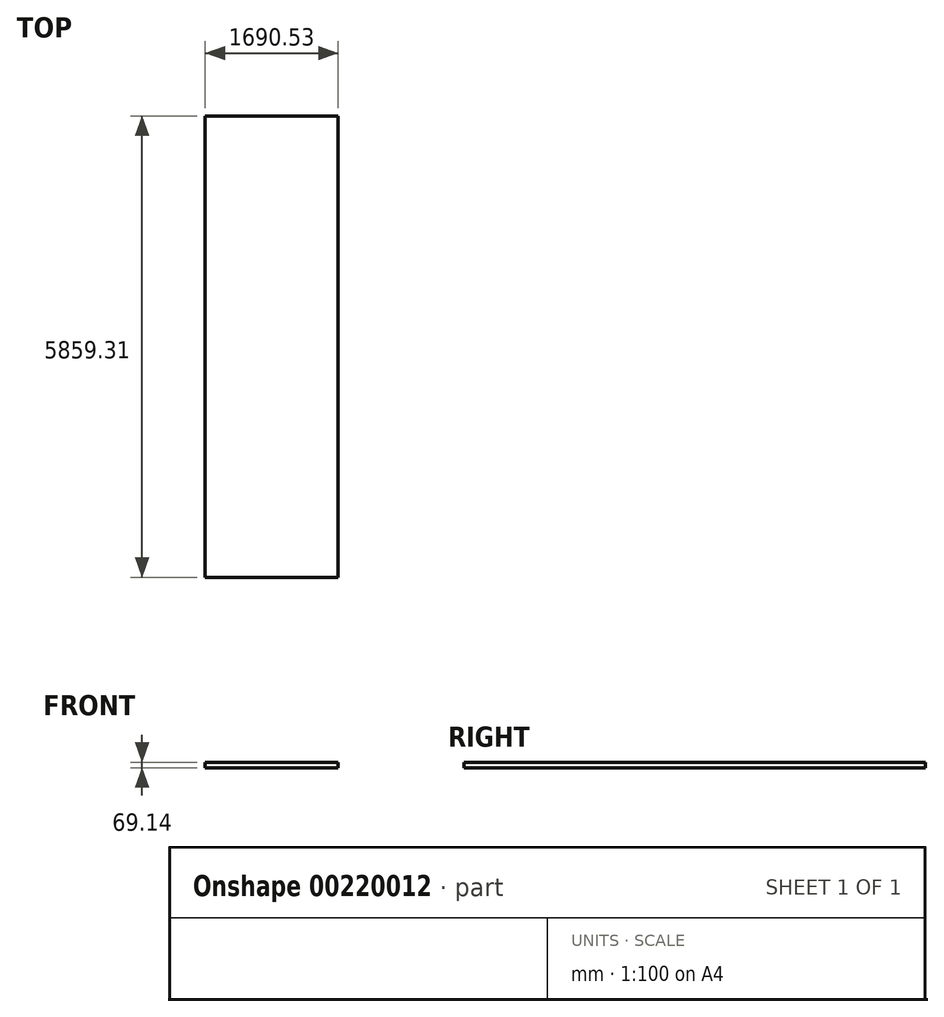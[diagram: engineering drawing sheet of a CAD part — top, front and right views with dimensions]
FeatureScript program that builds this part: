
annotation { "Feature Type Name" : "Feature", "Feature Type Description" : "" }
export const myFeature = defineFeature(function(context is Context, id is Id, definition is map)
    precondition{}
    {
        {
            var Q0;
            Q0=qCreatedBy(makeId("Top.planeOp"),FACE);
            var sketch = newSketch(context, id + "F0", { "sketchPlane" : qUnion([Q0])});
            skLineSegment(sketch, "E0.bottom", {"start": v(0, 0) * mm, "end": v(-1690.53, 0) * mm});
            skLineSegment(sketch, "E0.top", {"start": v(0, 5859.3) * mm, "end": v(-1690.53, 5859.3) * mm});
            skLineSegment(sketch, "E0.left", {"start": v(0, 0) * mm, "end": v(0, 5859.3) * mm});
            skLineSegment(sketch, "E0.right", {"start": v(-1690.53, 0) * mm, "end": v(-1690.53, 5859.3) * mm});
            skSolve(sketch);
        }
        {
            var Q0;
            Q0=makeQuery(id+"F0.imprint","IMPRINT",FACE,{"disambiguationData":[TD([[makeQuery(id+"F0.imprint","IMPRINT",EDGE,{"derivedFrom":sQuery(id+"F0.wireOp",EDGE,"E0.bottom")}),-1.0]])]});
            extrude(context, id + "F1", {"entities" : qUnion([Q0]), "depth" : 69.14 * mm});
        }
    });
